# Revit family: LTC-3RDW-CM
name_source: partatom
category: Lighting Fixtures
units: mm (PartAtom-declared; Revit-internal decimal feet)

## family parameters
Cut with Voids When Loaded = No
Host = Face
Light Source = Yes
OmniClass Number = 23.80.70.11.14.11
OmniClass Title = Downlights
Part Type = Normal
Room Calculation Point = No
Round Connector Dimension = Use Diameter
Shared = No

## types (1)
- LTC-3RDW-CM
    Apparent Load = 25 VA
    Ballast = Paint - Carbon Black
    Certifications = • cCSAus certified to UL 1598
• Wall Mount: Suitable for wet locations
• Surface & Pendant Mount: Suitable for wet
locations under covered ceiling
• Cord Mount and all Wall Wash: Suitable for
damp locations
    Color Filter = 16777215
    Cord Height = 72 "
    Default Elevation = 48 "
    Description = LITEISTRY™ 3inch Round Cylinder Downlight/Wall Wash
    Dimming Lamp Color Temperature Shift = <None>
    Emit Shape Visible in Rendering = No
    Emit from Circle Diameter = 6 "
    Features = 3inch architectural LED downlight and wall wash cylinder
delivering 600 - 2000 lm
• 4 beam distributions from 0.4 to 1.1 Spacing Criteria
• Quiet reflector appearance with 50º optical cutoff
• 2700K - 5000K, 80+ and 90+ CRI options
• Available in Surface, Wall, Pendant, or Cord Mount configurations
• Variety of dimming protocol options including 0-10V, DALI, DMX,
Lutron Forward Phase and EcoSystem
    Lamp = LED Lamp
    Manufacturer = Prescolite
    Model = LTC-3RDW
    Photometric Web File = LTC-3RD-P-20L35K8MD-DM1-S-BL.ies
    Reflector = Glass - Glass
    Tilt Angle = -90.00°
    URL = https://www.currentlighting.com
    Voltage = 120 V
    Warranty = 5 years warranty
    Wattage Comments = 8-25W

## geometry (parser evidence)
native form markers: Blend x11, Sweep x4
no freeform markers — native parametric forms only
